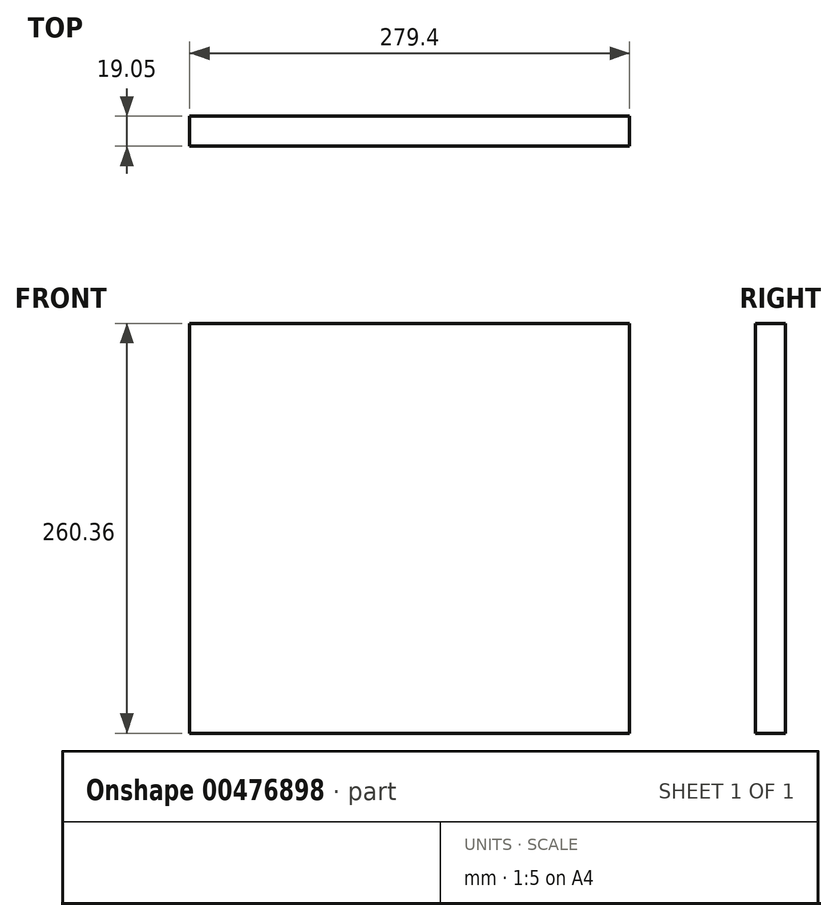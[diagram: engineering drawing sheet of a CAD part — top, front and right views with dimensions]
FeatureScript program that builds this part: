
annotation { "Feature Type Name" : "Feature", "Feature Type Description" : "" }
export const myFeature = defineFeature(function(context is Context, id is Id, definition is map)
    precondition{}
    {
        {
            var Q0;
            Q0=qCreatedBy(makeId("Front.planeOp"),FACE);
            var sketch = newSketch(context, id + "F0", { "sketchPlane" : qUnion([Q0])});
            skLineSegment(sketch, "E0.bottom", {"start": v(139.7, 130.18) * mm, "end": v(-139.7, 130.18) * mm});
            skLineSegment(sketch, "E0.top", {"start": v(139.7, -130.18) * mm, "end": v(-139.7, -130.18) * mm});
            skLineSegment(sketch, "E0.left", {"start": v(139.7, 130.18) * mm, "end": v(139.7, -130.17) * mm});
            skLineSegment(sketch, "E0.right", {"start": v(-139.7, 130.18) * mm, "end": v(-139.7, -130.18) * mm});
            skPoint(sketch, "E0.middle", {"position": v(0, 0) * mm});
            skSolve(sketch);
        }
        {
            var Q0;
            Q0 = qSketchRegion(id + "F0", true);
            extrude(context, id + "F1", {"entities" : qUnion([Q0]), "depth" : 19.05 * mm, "offsetDistance" : 25.4 * mm});
        }
    });
